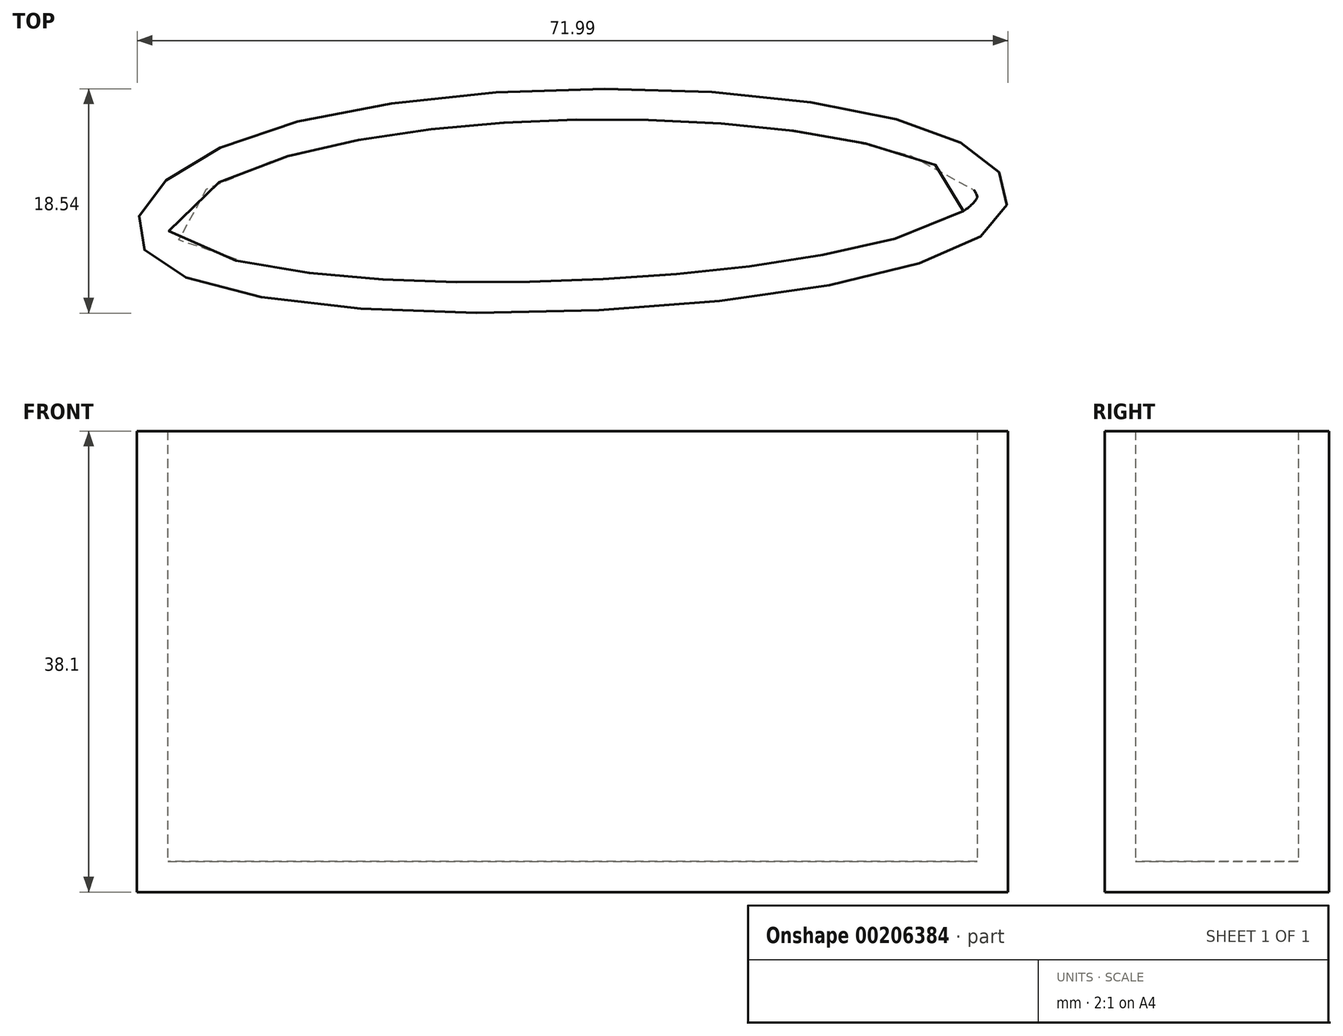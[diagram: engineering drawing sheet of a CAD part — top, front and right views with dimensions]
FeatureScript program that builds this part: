
annotation { "Feature Type Name" : "Feature", "Feature Type Description" : "" }
export const myFeature = defineFeature(function(context is Context, id is Id, definition is map)
    precondition{}
    {
        {
            var Q0;
            Q0=qCreatedBy(makeId("Top.planeOp"),FACE);
            var sketch = newSketch(context, id + "F0", { "sketchPlane" : qUnion([Q0])});
            skFitSpline(sketch, "E0", {"points": [v(-76.94, 25.75) * mm, v(-15.02, 25.75) * mm, v(-14.1, 18.4) * mm, v(-82.16, 16.25) * mm, v(-76.94, 25.75) * mm]});
            skSolve(sketch);
        }
        {
            var Q0;
            Q0 = qSketchRegion(id + "F0", true);
            extrude(context, id + "F1", {"entities" : qUnion([Q0]), "depth" : 38.1 * mm});
        }
        {
            var Q0;
            Q0=makeQuery(id+"F1.opExtrude","CAP_FACE",FACE,{"disambiguationData":[OSD([sQuery(id+"F0.wireOp",EDGE,"E0")])],"isStart":false});
            shell(context, id + "F2", {"entities" : qUnion([Q0]), "thickness" : 2.54 * mm});
        }
    });
